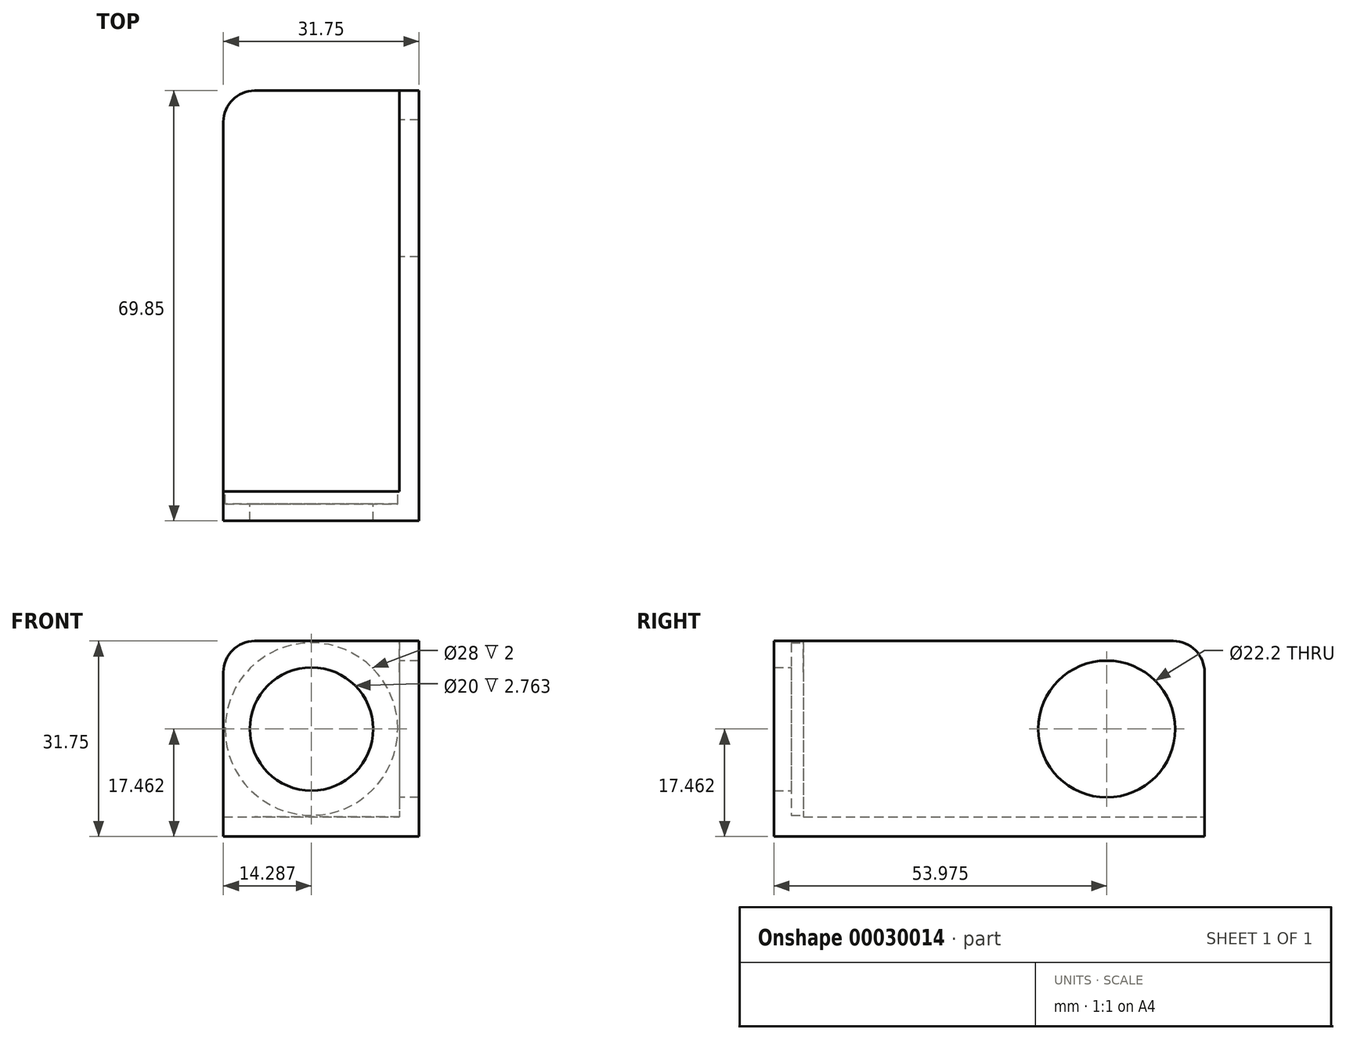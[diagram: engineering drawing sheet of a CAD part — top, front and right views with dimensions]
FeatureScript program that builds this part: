
annotation { "Feature Type Name" : "Feature", "Feature Type Description" : "" }
export const myFeature = defineFeature(function(context is Context, id is Id, definition is map)
    precondition{}
    {
        {
            var Q0;
            Q0=qCreatedBy(makeId("Front.planeOp"),FACE);
            var sketch = newSketch(context, id + "F0", { "sketchPlane" : qUnion([Q0])});
            skLineSegment(sketch, "E0", {"start": v(0, 0) * mm, "end": v(31.75, 0) * mm});
            skLineSegment(sketch, "E1", {"start": v(31.75, 0) * mm, "end": v(31.75, 31.75) * mm});
            skLineSegment(sketch, "E2", {"start": v(31.75, 31.75) * mm, "end": v(28.57, 31.75) * mm});
            skLineSegment(sketch, "E3", {"start": v(28.57, 31.75) * mm, "end": v(28.58, 3.18) * mm});
            skLineSegment(sketch, "E4", {"start": v(28.58, 3.18) * mm, "end": v(0, 3.18) * mm});
            skLineSegment(sketch, "E5", {"start": v(0, 3.18) * mm, "end": v(0, 0) * mm});
            skSolve(sketch);
        }
        {
            var Q0;
            Q0=qSketchRegion(id+"F0",true);
            extrude(context, id + "F1", {"entities" : qUnion([Q0]), "depth" : 69.85 * mm});
        }
        {
            var Q0;
            Q0=makeQuery(id+"F1.opExtrude","SWEPT_FACE",FACE,{"disambiguationData":[OSD([sQuery(id+"F0.wireOp",EDGE,"E4")])]});
            var sketch = newSketch(context, id + "F2", { "sketchPlane" : qUnion([Q0])});
            skLineSegment(sketch, "E6.bottom", {"start": v(0, -69.85) * mm, "end": v(28.58, -69.85) * mm});
            skLineSegment(sketch, "E6.top", {"start": v(0, -65.09) * mm, "end": v(28.58, -65.09) * mm});
            skLineSegment(sketch, "E6.left", {"start": v(0, -69.85) * mm, "end": v(0, -65.09) * mm});
            skLineSegment(sketch, "E6.right", {"start": v(28.58, -69.85) * mm, "end": v(28.58, -65.09) * mm});
            skSolve(sketch);
        }
        {
            var Q0;
            Q0=qSketchRegion(id+"F2",true);
            var Q1;
            Q1=makeQuery(id+"F1.opExtrude","SWEPT_FACE",FACE,{"disambiguationData":[OSD([sQuery(id+"F0.wireOp",EDGE,"E2")])]});
            extrude(context, id + "F3", {"entities" : qUnion([Q0]), "operationType" : NewBodyOperationType.ADD, "endBound" : BoundingType.UP_TO_SURFACE, "endBoundEntityFace" : qUnion([Q1]), "depth" : 25 * mm});
        }
        {
            var Q0;
            Q0=makeQuery(id+"F3.opExtrude","SWEPT_FACE",FACE,{"disambiguationData":[OSD([sQuery(id+"F2.wireOp",EDGE,"E6.top")])]});
            var sketch = newSketch(context, id + "F4", { "sketchPlane" : qUnion([Q0])});
            skLineSegment(sketch, "E7", {"start": v(-28.58, 17.46) * mm, "end": v(0, 17.46) * mm, "construction": true});
            skCircle(sketch, "E8", {"center": v(-14.29, 17.46) * mm, "radius": 14 * mm});
            skSolve(sketch);
        }
        {
            var Q0;
            Q0=qSketchRegion(id+"F4",true);
            extrude(context, id + "F5", {"entities" : qUnion([Q0]), "operationType" : NewBodyOperationType.REMOVE, "oppositeDirection" : true, "depth" : 2 * mm});
        }
        {
            var Q0;
            Q0=makeQuery(id+"F5.boolean.opBoolean","COPY",FACE,{"derivedFrom":makeQuery(id+"F5.opExtrude","CAP_FACE",FACE,{"disambiguationData":[OSD([sQuery(id+"F4.wireOp",EDGE,"E8")])],"isStart":false})});
            var sketch = newSketch(context, id + "F6", { "sketchPlane" : qUnion([Q0])});
            skCircle(sketch, "E9", {"center": v(-14.29, 17.46) * mm, "radius": 10 * mm});
            skSolve(sketch);
        }
        {
            var Q0;
            Q0=qSketchRegion(id+"F6",true);
            extrude(context, id + "F7", {"entities" : qUnion([Q0]), "operationType" : NewBodyOperationType.REMOVE, "endBound" : BoundingType.UP_TO_NEXT, "oppositeDirection" : true, "depth" : 25 * mm});
        }
        {
            var Q0;
            Q0=makeQuery(id+"F1.opExtrude","SWEPT_FACE",FACE,{"disambiguationData":[OSD([sQuery(id+"F0.wireOp",EDGE,"E3")])]});
            var sketch = newSketch(context, id + "F8", { "sketchPlane" : qUnion([Q0])});
            skPoint(sketch, "E10", {"position": v(15.88, 17.46) * mm});
            skCircle(sketch, "E11", {"center": v(15.88, 17.46) * mm, "radius": 11.1 * mm});
            skLineSegment(sketch, "E12", {"start": v(65.09, 17.46) * mm, "end": v(0, 17.46) * mm});
            skSolve(sketch);
        }
        {
            var Q0;
            Q0=qSketchRegion(id+"F8",true);
            extrude(context, id + "F9", {"entities" : qUnion([Q0]), "operationType" : NewBodyOperationType.REMOVE, "endBound" : BoundingType.UP_TO_NEXT, "oppositeDirection" : true, "depth" : 25 * mm});
        }
        {
            var Q0;
            Q0=makeQuery(id+"F1.opExtrude","CAP_EDGE",EDGE,{"disambiguationData":[OSD([sQuery(id+"F0.wireOp",EDGE,"E5")])],"isStart":true});
            var Q1;
            Q1=makeQuery(id+"F3.opExtrude","CAP_EDGE",EDGE,{"disambiguationData":[OSD([sQuery(id+"F2.wireOp",EDGE,"E6.left")])],"isStart":false});
            var Q2;
            Q2=makeQuery(id+"F1.opExtrude","CAP_EDGE",EDGE,{"disambiguationData":[OSD([sQuery(id+"F0.wireOp",EDGE,"E2")])],"isStart":true});
            fillet(context, id + "F10", {"entities" : qUnion([Q0, Q1, Q2]), "radius" : 5.08 * mm, "tangentPropagation" : true, "allowEdgeOverflow" : false});
        }
    });
